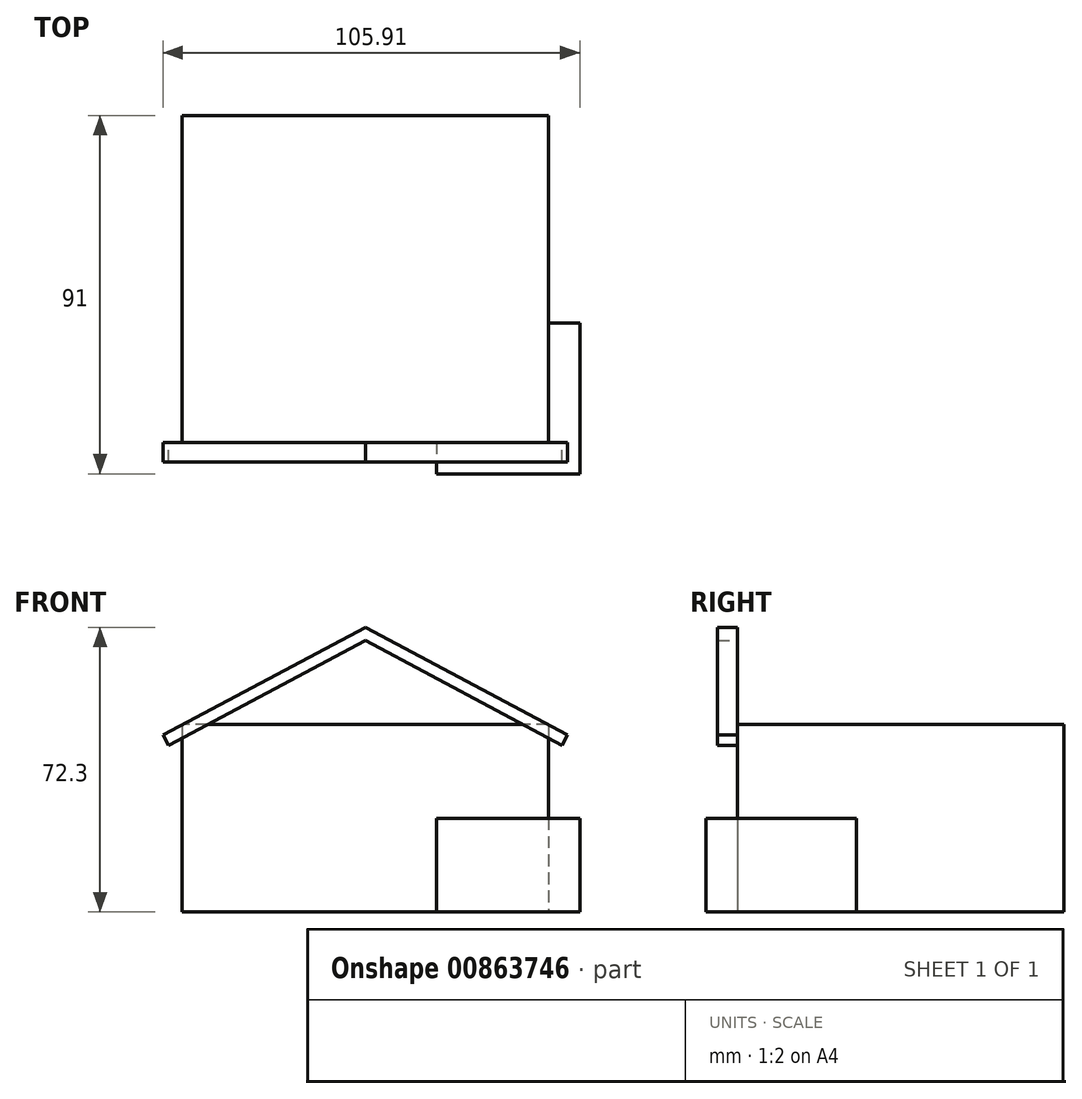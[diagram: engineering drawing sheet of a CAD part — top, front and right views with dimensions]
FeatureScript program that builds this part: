
annotation { "Feature Type Name" : "Feature", "Feature Type Description" : "" }
export const myFeature = defineFeature(function(context is Context, id is Id, definition is map)
    precondition{}
    {
        {
            var Q0;
            Q0=qCreatedBy(makeId("Top.planeOp"),FACE);
            var sketch = newSketch(context, id + "F0", { "sketchPlane" : qUnion([Q0])});
            skLineSegment(sketch, "E0.bottom", {"start": v(46.5, -41.5) * mm, "end": v(-46.5, -41.5) * mm});
            skLineSegment(sketch, "E0.top", {"start": v(46.5, 41.5) * mm, "end": v(-46.5, 41.5) * mm});
            skLineSegment(sketch, "E0.left", {"start": v(46.5, -41.5) * mm, "end": v(46.5, 41.5) * mm});
            skLineSegment(sketch, "E0.right", {"start": v(-46.5, -41.5) * mm, "end": v(-46.5, 41.5) * mm});
            skPoint(sketch, "E0.middle", {"position": v(0, 0) * mm});
            skPoint(sketch, "E1.orphan", {"position": v(46.5, -41.5) * mm});
            skSolve(sketch);
        }
        {
            var Q0;
            Q0 = qSketchRegion(id + "F0", true);
            extrude(context, id + "F1", {"entities" : qUnion([Q0]), "depth" : 47.6 * mm, "offsetDistance" : 25 * mm});
        }
        {
            var Q0;
            Q0=qCreatedBy(makeId("Top.planeOp"),FACE);
            var sketch = newSketch(context, id + "F2", { "sketchPlane" : qUnion([Q0])});
            skLineSegment(sketch, "E2", {"start": v(18.1, -41.5) * mm, "end": v(18.1, -49.5) * mm});
            skLineSegment(sketch, "E3", {"start": v(18.1, -49.5) * mm, "end": v(54.5, -49.5) * mm});
            skLineSegment(sketch, "E4", {"start": v(54.5, -49.5) * mm, "end": v(54.5, -11.2) * mm});
            skLineSegment(sketch, "E5", {"start": v(54.5, -11.2) * mm, "end": v(46.5, -11.2) * mm});
            skLineSegment(sketch, "E6", {"start": v(46.5, -11.2) * mm, "end": v(46.5, -41.5) * mm});
            skLineSegment(sketch, "E7", {"start": v(46.5, -41.5) * mm, "end": v(18.1, -41.5) * mm});
            skSolve(sketch);
        }
        {
            var Q0;
            Q0 = qSketchRegion(id + "F2", true);
            extrude(context, id + "F3", {"entities" : qUnion([Q0]), "operationType" : NewBodyOperationType.ADD, "depth" : 23.8 * mm, "offsetDistance" : 25 * mm});
        }
        {
            var Q0;
            Q0=qCreatedBy(makeId("Front.planeOp"),FACE);
            var sketch = newSketch(context, id + "F4", { "sketchPlane" : qUnion([Q0])});
            skLineSegment(sketch, "E8", {"start": v(0, 72.3) * mm, "end": v(-51.4, 45) * mm});
            skLineSegment(sketch, "E9", {"start": v(50, 42.34) * mm, "end": v(51.4, 45) * mm});
            skLineSegment(sketch, "E10", {"start": v(51.4, 45) * mm, "end": v(0, 72.3) * mm});
            skLineSegment(sketch, "E11", {"start": v(-51.4, 45) * mm, "end": v(-50, 42.34) * mm});
            skLineSegment(sketch, "E12", {"start": v(-50, 42.34) * mm, "end": v(-40.1, 47.6) * mm});
            skLineSegment(sketch, "E13", {"start": v(40.1, 47.6) * mm, "end": v(50, 42.34) * mm});
            skLineSegment(sketch, "E14", {"start": v(-40.1, 47.6) * mm, "end": v(40.1, 47.6) * mm});
            skPoint(sketch, "E15.orphan", {"position": v(0, 68.9) * mm});
            skSolve(sketch);
        }
        {
            var Q0;
            {var subQ0=sQuery(id+"F0.wireOp",EDGE,"E0.bottom");Q0=makeQuery(id+"FiI2U1FCMb0vBwo_1.boolean.opBoolean","MERGE",FACE,{"derivedFrom":[makeQuery(id+"F1.opExtrude","SWEPT_FACE",FACE,{"disambiguationData":[OSD([subQ0])]}),makeQuery(id+"FiI2U1FCMb0vBwo_1.opExtrude","CAP_FACE",FACE,{"disambiguationData":[OSD([subQ0])],"isStart":false})]});}
            var sketch = newSketch(context, id + "F5", { "sketchPlane" : qUnion([Q0])});
            skLineSegment(sketch, "E16.0", {"start": v(0, 72.3) * mm, "end": v(-51.4, 45) * mm});
            skLineSegment(sketch, "E16.1", {"start": v(-51.4, 45) * mm, "end": v(-50, 42.34) * mm});
            skLineSegment(sketch, "E16.2", {"start": v(-50, 42.34) * mm, "end": v(0, 68.9) * mm});
            skLineSegment(sketch, "E16.3", {"start": v(51.4, 45) * mm, "end": v(0, 72.3) * mm});
            skLineSegment(sketch, "E16.4", {"start": v(50, 42.34) * mm, "end": v(51.4, 45) * mm});
            skLineSegment(sketch, "E16.5", {"start": v(0, 68.9) * mm, "end": v(50, 42.34) * mm});
            skPoint(sketch, "E17.orphan", {"position": v(-46.5, 44.2) * mm});
            skPoint(sketch, "E18.orphan", {"position": v(46.5, 44.2) * mm});
            skSolve(sketch);
        }
        {
            var Q0;
            Q0 = qSketchRegion(id + "F5", true);
            extrude(context, id + "F6", {"entities" : qUnion([Q0]), "operationType" : NewBodyOperationType.ADD, "depth" : 5 * mm, "offsetDistance" : 25 * mm});
        }
    });
